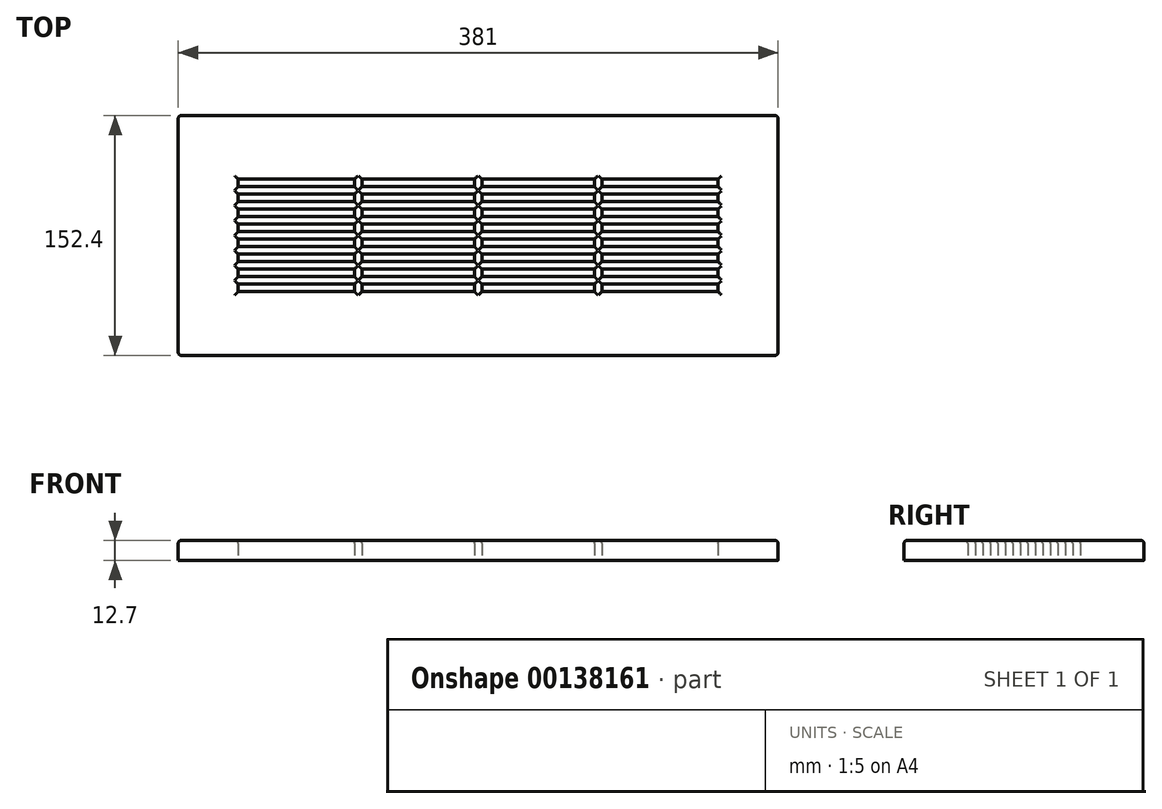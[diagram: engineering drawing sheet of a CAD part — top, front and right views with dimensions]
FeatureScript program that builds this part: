
annotation { "Feature Type Name" : "Feature", "Feature Type Description" : "" }
export const myFeature = defineFeature(function(context is Context, id is Id, definition is map)
    precondition{}
    {
        {
            var Q0;
            Q0=qCreatedBy(makeId("Top.planeOp"),FACE);
            var sketch = newSketch(context, id + "F0", { "sketchPlane" : qUnion([Q0])});
            skLineSegment(sketch, "E0.bottom", {"start": v(-152.4, 38.1) * mm, "end": v(152.4, 38.1) * mm});
            skLineSegment(sketch, "E0.top", {"start": v(-152.4, -38.1) * mm, "end": v(152.4, -38.1) * mm});
            skLineSegment(sketch, "E0.left", {"start": v(-152.4, 38.1) * mm, "end": v(-152.4, -38.1) * mm});
            skLineSegment(sketch, "E0.right", {"start": v(152.4, 38.1) * mm, "end": v(152.4, -38.1) * mm});
            skPoint(sketch, "E0.middle", {"position": v(0, 0) * mm});
            skLineSegment(sketch, "E1.bottom", {"start": v(-190.5, 76.2) * mm, "end": v(190.5, 76.2) * mm});
            skLineSegment(sketch, "E1.top", {"start": v(-190.5, -76.2) * mm, "end": v(190.5, -76.2) * mm});
            skLineSegment(sketch, "E1.left", {"start": v(-190.5, 76.2) * mm, "end": v(-190.5, -76.2) * mm});
            skLineSegment(sketch, "E1.right", {"start": v(190.5, 76.2) * mm, "end": v(190.5, -76.2) * mm});
            skPoint(sketch, "E2", {"position": v(-152.4, 0) * mm});
            skPoint(sketch, "E3", {"position": v(152.4, 0) * mm});
            skPoint(sketch, "E4", {"position": v(-152.4, 19.05) * mm});
            skPoint(sketch, "E5", {"position": v(152.4, 19.05) * mm});
            skPoint(sketch, "E6", {"position": v(-152.4, -19.05) * mm});
            skPoint(sketch, "E7", {"position": v(152.4, -19.05) * mm});
            skLineSegment(sketch, "E8", {"start": v(-152.4, 0) * mm, "end": v(152.4, 0) * mm, "construction": true});
            skLineSegment(sketch, "E9", {"start": v(-152.4, 19.05) * mm, "end": v(152.4, 19.05) * mm, "construction": true});
            skLineSegment(sketch, "E10", {"start": v(-152.4, -19.05) * mm, "end": v(152.4, -19.05) * mm, "construction": true});
            skPoint(sketch, "E11", {"position": v(152.4, 28.58) * mm});
            skPoint(sketch, "E12", {"position": v(-152.4, 28.58) * mm});
            skPoint(sketch, "E13", {"position": v(152.4, 9.53) * mm});
            skPoint(sketch, "E14", {"position": v(-152.4, 9.53) * mm});
            skPoint(sketch, "E15", {"position": v(152.4, -9.53) * mm});
            skPoint(sketch, "E16", {"position": v(-152.4, -9.53) * mm});
            skPoint(sketch, "E17", {"position": v(152.4, -28.58) * mm});
            skPoint(sketch, "E18", {"position": v(-152.4, -28.58) * mm});
            skLineSegment(sketch, "E19", {"start": v(-152.4, 28.58) * mm, "end": v(152.4, 28.58) * mm, "construction": true});
            skLineSegment(sketch, "E20", {"start": v(152.4, 9.53) * mm, "end": v(-152.4, 9.53) * mm, "construction": true});
            skLineSegment(sketch, "E21", {"start": v(-152.4, -9.53) * mm, "end": v(152.4, -9.53) * mm, "construction": true});
            skLineSegment(sketch, "E22", {"start": v(152.4, -28.58) * mm, "end": v(-152.4, -28.58) * mm, "construction": true});
            skPoint(sketch, "E23", {"position": v(-152.4, 30.96) * mm});
            skPoint(sketch, "E24", {"position": v(152.4, 30.96) * mm});
            skPoint(sketch, "E25", {"position": v(152.4, 26.2) * mm});
            skPoint(sketch, "E26", {"position": v(-152.4, 26.2) * mm});
            skLineSegment(sketch, "E27", {"start": v(-152.4, 30.96) * mm, "end": v(152.4, 30.96) * mm});
            skLineSegment(sketch, "E28", {"start": v(-152.4, 26.2) * mm, "end": v(152.4, 26.2) * mm});
            skPoint(sketch, "E29", {"position": v(152.4, 21.43) * mm});
            skPoint(sketch, "E30", {"position": v(-152.4, 21.43) * mm});
            skPoint(sketch, "E31", {"position": v(152.4, 16.67) * mm});
            skPoint(sketch, "E32", {"position": v(-152.4, 16.67) * mm});
            skLineSegment(sketch, "E33", {"start": v(-152.4, 21.43) * mm, "end": v(152.4, 21.43) * mm});
            skLineSegment(sketch, "E34", {"start": v(152.4, 16.67) * mm, "end": v(-152.4, 16.67) * mm});
            skPoint(sketch, "E35", {"position": v(152.4, 11.9) * mm});
            skPoint(sketch, "E36", {"position": v(-152.4, 11.9) * mm});
            skPoint(sketch, "E37", {"position": v(-152.4, 7.14) * mm});
            skPoint(sketch, "E38", {"position": v(152.4, 7.14) * mm});
            skPoint(sketch, "E39", {"position": v(152.4, -2.38) * mm});
            skPoint(sketch, "E40", {"position": v(-152.4, -2.38) * mm});
            skPoint(sketch, "E41", {"position": v(-152.4, -11.9) * mm});
            skPoint(sketch, "E42", {"position": v(152.4, -11.9) * mm});
            skPoint(sketch, "E43", {"position": v(152.4, -21.43) * mm});
            skPoint(sketch, "E44", {"position": v(-152.4, -21.43) * mm});
            skPoint(sketch, "E45", {"position": v(-152.4, -30.96) * mm});
            skPoint(sketch, "E46", {"position": v(152.4, -30.96) * mm});
            skPoint(sketch, "E47", {"position": v(152.4, 2.38) * mm});
            skPoint(sketch, "E48", {"position": v(-152.4, 2.38) * mm});
            skPoint(sketch, "E49", {"position": v(-152.4, -7.14) * mm});
            skPoint(sketch, "E50", {"position": v(152.4, -7.14) * mm});
            skPoint(sketch, "E51", {"position": v(152.4, -16.67) * mm});
            skPoint(sketch, "E52", {"position": v(-152.4, -16.67) * mm});
            skPoint(sketch, "E53", {"position": v(-152.4, -26.2) * mm});
            skPoint(sketch, "E54", {"position": v(152.4, -26.2) * mm});
            skLineSegment(sketch, "E55", {"start": v(152.4, 11.9) * mm, "end": v(-152.4, 11.9) * mm});
            skLineSegment(sketch, "E56", {"start": v(-152.4, 7.14) * mm, "end": v(152.4, 7.14) * mm});
            skLineSegment(sketch, "E57", {"start": v(152.4, 2.38) * mm, "end": v(-152.4, 2.38) * mm});
            skLineSegment(sketch, "E58", {"start": v(-152.4, -2.38) * mm, "end": v(152.4, -2.38) * mm});
            skLineSegment(sketch, "E59", {"start": v(152.4, -7.14) * mm, "end": v(-152.4, -7.14) * mm});
            skLineSegment(sketch, "E60", {"start": v(-152.4, -11.9) * mm, "end": v(152.4, -11.9) * mm});
            skLineSegment(sketch, "E61", {"start": v(152.4, -16.67) * mm, "end": v(-152.4, -16.67) * mm});
            skLineSegment(sketch, "E62", {"start": v(-152.4, -21.43) * mm, "end": v(152.4, -21.43) * mm});
            skLineSegment(sketch, "E63", {"start": v(152.4, -26.2) * mm, "end": v(-152.4, -26.2) * mm});
            skLineSegment(sketch, "E64", {"start": v(-152.4, -30.96) * mm, "end": v(152.4, -30.96) * mm});
            skPoint(sketch, "E65", {"position": v(-152.4, 35.72) * mm});
            skPoint(sketch, "E66", {"position": v(152.4, 35.72) * mm});
            skPoint(sketch, "E67", {"position": v(152.4, -35.72) * mm});
            skPoint(sketch, "E68", {"position": v(-152.4, -35.72) * mm});
            skLineSegment(sketch, "E69", {"start": v(152.4, 35.72) * mm, "end": v(-152.4, 35.72) * mm});
            skLineSegment(sketch, "E70", {"start": v(-152.4, -35.72) * mm, "end": v(152.4, -35.72) * mm});
            skPoint(sketch, "E71", {"position": v(0, 38.1) * mm});
            skPoint(sketch, "E72", {"position": v(0, -38.1) * mm});
            skLineSegment(sketch, "E73", {"start": v(0, 38.1) * mm, "end": v(0, -38.1) * mm, "construction": true});
            skPoint(sketch, "E74", {"position": v(2.38, 38.1) * mm});
            skPoint(sketch, "E75", {"position": v(2.38, -38.1) * mm});
            skPoint(sketch, "E76", {"position": v(-2.38, -38.1) * mm});
            skPoint(sketch, "E77", {"position": v(-2.38, 38.1) * mm});
            skLineSegment(sketch, "E78", {"start": v(-2.38, 38.1) * mm, "end": v(-2.38, -38.1) * mm});
            skLineSegment(sketch, "E79", {"start": v(2.38, 38.1) * mm, "end": v(2.38, -38.1) * mm});
            skPoint(sketch, "E80", {"position": v(76.2, 38.1) * mm});
            skPoint(sketch, "E81", {"position": v(76.2, -38.1) * mm});
            skPoint(sketch, "E82", {"position": v(-76.2, -38.1) * mm});
            skPoint(sketch, "E83", {"position": v(-76.2, 38.1) * mm});
            skPoint(sketch, "E84", {"position": v(-78.58, 38.1) * mm});
            skPoint(sketch, "E85", {"position": v(-78.58, -38.1) * mm});
            skPoint(sketch, "E86", {"position": v(-73.82, 38.1) * mm});
            skPoint(sketch, "E87", {"position": v(-73.82, -38.1) * mm});
            skPoint(sketch, "E88", {"position": v(73.82, 38.1) * mm});
            skPoint(sketch, "E89", {"position": v(73.82, -38.1) * mm});
            skPoint(sketch, "E90", {"position": v(78.58, 38.1) * mm});
            skPoint(sketch, "E91", {"position": v(78.58, -38.1) * mm});
            skLineSegment(sketch, "E92", {"start": v(-78.58, 38.1) * mm, "end": v(-78.58, -38.1) * mm});
            skLineSegment(sketch, "E93", {"start": v(-73.82, 38.1) * mm, "end": v(-73.82, -38.1) * mm});
            skLineSegment(sketch, "E94", {"start": v(73.82, 38.1) * mm, "end": v(73.82, -38.1) * mm});
            skLineSegment(sketch, "E95", {"start": v(78.58, 38.1) * mm, "end": v(78.58, -38.1) * mm});
            skSolve(sketch);
        }
        {
            var Q0;
            {var subQ7=sQuery(id+"F0.wireOp",EDGE,"E0.bottom");Q0=makeQuery(id+"F0.imprint","IMPRINT",FACE,{"disambiguationData":[TD([[makeQuery(id+"F0.imprint","IMPRINT",EDGE,{"derivedFrom":subQ7}),1.0]])]});}
            var Q1;
            {var subQ0=sQuery(id+"F0.wireOp",EDGE,"E0.bottom");Q1=makeQuery(id+"F0.imprint","IMPRINT",FACE,{"disambiguationData":[TD([[makeQuery(id+"F0.imprint","IMPRINT",EDGE,{"derivedFrom":subQ0}),-1.0]])]});}
            var Q2;
            {var subQ0=sQuery(id+"F0.wireOp",EDGE,"E0.top");Q2=makeQuery(id+"F0.imprint","IMPRINT",FACE,{"disambiguationData":[TD([[makeQuery(id+"F0.imprint","IMPRINT",EDGE,{"derivedFrom":subQ0}),1.0]])]});}
            var Q3;
            {var subQ0=sQuery(id+"F0.wireOp",EDGE,"E63");Q3=makeQuery(id+"F0.imprint","IMPRINT",FACE,{"disambiguationData":[TD([[makeQuery(id+"F0.imprint","IMPRINT",EDGE,{"derivedFrom":subQ0}),1.0]])]});}
            var Q4;
            {var subQ0=sQuery(id+"F0.wireOp",EDGE,"E61");Q4=makeQuery(id+"F0.imprint","IMPRINT",FACE,{"disambiguationData":[TD([[makeQuery(id+"F0.imprint","IMPRINT",EDGE,{"derivedFrom":subQ0}),1.0]])]});}
            var Q5;
            {var subQ0=sQuery(id+"F0.wireOp",EDGE,"E59");Q5=makeQuery(id+"F0.imprint","IMPRINT",FACE,{"disambiguationData":[TD([[makeQuery(id+"F0.imprint","IMPRINT",EDGE,{"derivedFrom":subQ0}),1.0]])]});}
            var Q6;
            {var subQ0=sQuery(id+"F0.wireOp",EDGE,"E57");Q6=makeQuery(id+"F0.imprint","IMPRINT",FACE,{"disambiguationData":[TD([[makeQuery(id+"F0.imprint","IMPRINT",EDGE,{"derivedFrom":subQ0}),1.0]])]});}
            var Q7;
            {var subQ0=sQuery(id+"F0.wireOp",EDGE,"E55");Q7=makeQuery(id+"F0.imprint","IMPRINT",FACE,{"disambiguationData":[TD([[makeQuery(id+"F0.imprint","IMPRINT",EDGE,{"derivedFrom":subQ0}),1.0]])]});}
            var Q8;
            {var subQ0=sQuery(id+"F0.wireOp",EDGE,"E33");Q8=makeQuery(id+"F0.imprint","IMPRINT",FACE,{"disambiguationData":[TD([[makeQuery(id+"F0.imprint","IMPRINT",EDGE,{"derivedFrom":subQ0}),-1.0]])]});}
            var Q9;
            {var subQ0=sQuery(id+"F0.wireOp",EDGE,"E27");Q9=makeQuery(id+"F0.imprint","IMPRINT",FACE,{"disambiguationData":[TD([[makeQuery(id+"F0.imprint","IMPRINT",EDGE,{"derivedFrom":subQ0}),-1.0]])]});}
            var Q10;
            {var subQ0=sQuery(id+"F0.wireOp",EDGE,"E92");var subQ1=sQuery(id+"F0.wireOp",EDGE,"E27");var subQ2=makeQuery(id+"F0.imprint","INTERSECT",VERTEX,{"derivedFrom":[subQ1,subQ0]});Q10=makeQuery(id+"F0.imprint","IMPRINT",FACE,{"disambiguationData":[TD([[makeQuery(id+"F0.imprint","IMPRINT",EDGE,{"disambiguationData":[TD([[subQ2,-1.0]])],"derivedFrom":subQ1}),1.0]])]});}
            var Q11;
            {var subQ0=sQuery(id+"F0.wireOp",EDGE,"E92");var subQ1=sQuery(id+"F0.wireOp",EDGE,"E28");var subQ2=makeQuery(id+"F0.imprint","INTERSECT",VERTEX,{"derivedFrom":[subQ1,subQ0]});Q11=makeQuery(id+"F0.imprint","IMPRINT",FACE,{"disambiguationData":[TD([[makeQuery(id+"F0.imprint","IMPRINT",EDGE,{"disambiguationData":[TD([[subQ2,-1.0]])],"derivedFrom":subQ1}),-1.0]])]});}
            var Q12;
            {var subQ0=sQuery(id+"F0.wireOp",EDGE,"E93");var subQ1=sQuery(id+"F0.wireOp",EDGE,"E34");var subQ2=makeQuery(id+"F0.imprint","INTERSECT",VERTEX,{"derivedFrom":[subQ1,subQ0]});Q12=makeQuery(id+"F0.imprint","IMPRINT",FACE,{"disambiguationData":[TD([[makeQuery(id+"F0.imprint","IMPRINT",EDGE,{"disambiguationData":[TD([[subQ2,-1.0]])],"derivedFrom":subQ1}),1.0]])]});}
            var Q13;
            {var subQ0=sQuery(id+"F0.wireOp",EDGE,"E92");var subQ1=sQuery(id+"F0.wireOp",EDGE,"E56");var subQ2=makeQuery(id+"F0.imprint","INTERSECT",VERTEX,{"derivedFrom":[subQ1,subQ0]});Q13=makeQuery(id+"F0.imprint","IMPRINT",FACE,{"disambiguationData":[TD([[makeQuery(id+"F0.imprint","IMPRINT",EDGE,{"disambiguationData":[TD([[subQ2,-1.0]])],"derivedFrom":subQ1}),-1.0]])]});}
            var Q14;
            {var subQ0=sQuery(id+"F0.wireOp",EDGE,"E92");var subQ1=sQuery(id+"F0.wireOp",EDGE,"E58");var subQ2=makeQuery(id+"F0.imprint","INTERSECT",VERTEX,{"derivedFrom":[subQ1,subQ0]});Q14=makeQuery(id+"F0.imprint","IMPRINT",FACE,{"disambiguationData":[TD([[makeQuery(id+"F0.imprint","IMPRINT",EDGE,{"disambiguationData":[TD([[subQ2,-1.0]])],"derivedFrom":subQ1}),-1.0]])]});}
            var Q15;
            {var subQ0=sQuery(id+"F0.wireOp",EDGE,"E92");var subQ1=sQuery(id+"F0.wireOp",EDGE,"E60");var subQ2=makeQuery(id+"F0.imprint","INTERSECT",VERTEX,{"derivedFrom":[subQ1,subQ0]});Q15=makeQuery(id+"F0.imprint","IMPRINT",FACE,{"disambiguationData":[TD([[makeQuery(id+"F0.imprint","IMPRINT",EDGE,{"disambiguationData":[TD([[subQ2,-1.0]])],"derivedFrom":subQ1}),-1.0]])]});}
            var Q16;
            {var subQ0=sQuery(id+"F0.wireOp",EDGE,"E92");var subQ1=sQuery(id+"F0.wireOp",EDGE,"E62");var subQ2=makeQuery(id+"F0.imprint","INTERSECT",VERTEX,{"derivedFrom":[subQ1,subQ0]});Q16=makeQuery(id+"F0.imprint","IMPRINT",FACE,{"disambiguationData":[TD([[makeQuery(id+"F0.imprint","IMPRINT",EDGE,{"disambiguationData":[TD([[subQ2,-1.0]])],"derivedFrom":subQ1}),-1.0]])]});}
            var Q17;
            {var subQ0=sQuery(id+"F0.wireOp",EDGE,"E92");var subQ1=sQuery(id+"F0.wireOp",EDGE,"E64");var subQ2=makeQuery(id+"F0.imprint","INTERSECT",VERTEX,{"derivedFrom":[subQ1,subQ0]});Q17=makeQuery(id+"F0.imprint","IMPRINT",FACE,{"disambiguationData":[TD([[makeQuery(id+"F0.imprint","IMPRINT",EDGE,{"disambiguationData":[TD([[subQ2,-1.0]])],"derivedFrom":subQ1}),-1.0]])]});}
            var Q18;
            {var subQ0=sQuery(id+"F0.wireOp",EDGE,"E78");var subQ1=sQuery(id+"F0.wireOp",EDGE,"E64");var subQ2=makeQuery(id+"F0.imprint","INTERSECT",VERTEX,{"derivedFrom":[subQ1,subQ0]});Q18=makeQuery(id+"F0.imprint","IMPRINT",FACE,{"disambiguationData":[TD([[makeQuery(id+"F0.imprint","IMPRINT",EDGE,{"disambiguationData":[TD([[subQ2,-1.0]])],"derivedFrom":subQ1}),-1.0]])]});}
            var Q19;
            {var subQ0=sQuery(id+"F0.wireOp",EDGE,"E78");var subQ1=sQuery(id+"F0.wireOp",EDGE,"E62");var subQ2=makeQuery(id+"F0.imprint","INTERSECT",VERTEX,{"derivedFrom":[subQ1,subQ0]});Q19=makeQuery(id+"F0.imprint","IMPRINT",FACE,{"disambiguationData":[TD([[makeQuery(id+"F0.imprint","IMPRINT",EDGE,{"disambiguationData":[TD([[subQ2,-1.0]])],"derivedFrom":subQ1}),-1.0]])]});}
            var Q20;
            {var subQ0=sQuery(id+"F0.wireOp",EDGE,"E79");var subQ1=sQuery(id+"F0.wireOp",EDGE,"E34");var subQ2=makeQuery(id+"F0.imprint","INTERSECT",VERTEX,{"derivedFrom":[subQ1,subQ0]});Q20=makeQuery(id+"F0.imprint","IMPRINT",FACE,{"disambiguationData":[TD([[makeQuery(id+"F0.imprint","IMPRINT",EDGE,{"disambiguationData":[TD([[subQ2,-1.0]])],"derivedFrom":subQ1}),1.0]])]});}
            var Q21;
            {var subQ0=sQuery(id+"F0.wireOp",EDGE,"E78");var subQ1=sQuery(id+"F0.wireOp",EDGE,"E28");var subQ2=makeQuery(id+"F0.imprint","INTERSECT",VERTEX,{"derivedFrom":[subQ1,subQ0]});Q21=makeQuery(id+"F0.imprint","IMPRINT",FACE,{"disambiguationData":[TD([[makeQuery(id+"F0.imprint","IMPRINT",EDGE,{"disambiguationData":[TD([[subQ2,-1.0]])],"derivedFrom":subQ1}),-1.0]])]});}
            var Q22;
            {var subQ0=sQuery(id+"F0.wireOp",EDGE,"E78");var subQ1=sQuery(id+"F0.wireOp",EDGE,"E27");var subQ2=makeQuery(id+"F0.imprint","INTERSECT",VERTEX,{"derivedFrom":[subQ1,subQ0]});Q22=makeQuery(id+"F0.imprint","IMPRINT",FACE,{"disambiguationData":[TD([[makeQuery(id+"F0.imprint","IMPRINT",EDGE,{"disambiguationData":[TD([[subQ2,-1.0]])],"derivedFrom":subQ1}),1.0]])]});}
            var Q23;
            {var subQ0=sQuery(id+"F0.wireOp",EDGE,"E94");var subQ1=sQuery(id+"F0.wireOp",EDGE,"E27");var subQ2=makeQuery(id+"F0.imprint","INTERSECT",VERTEX,{"derivedFrom":[subQ1,subQ0]});Q23=makeQuery(id+"F0.imprint","IMPRINT",FACE,{"disambiguationData":[TD([[makeQuery(id+"F0.imprint","IMPRINT",EDGE,{"disambiguationData":[TD([[subQ2,-1.0]])],"derivedFrom":subQ1}),1.0]])]});}
            var Q24;
            {var subQ0=sQuery(id+"F0.wireOp",EDGE,"E94");var subQ1=sQuery(id+"F0.wireOp",EDGE,"E28");var subQ2=makeQuery(id+"F0.imprint","INTERSECT",VERTEX,{"derivedFrom":[subQ1,subQ0]});Q24=makeQuery(id+"F0.imprint","IMPRINT",FACE,{"disambiguationData":[TD([[makeQuery(id+"F0.imprint","IMPRINT",EDGE,{"disambiguationData":[TD([[subQ2,-1.0]])],"derivedFrom":subQ1}),-1.0]])]});}
            var Q25;
            {var subQ0=sQuery(id+"F0.wireOp",EDGE,"E95");var subQ1=sQuery(id+"F0.wireOp",EDGE,"E34");var subQ2=makeQuery(id+"F0.imprint","INTERSECT",VERTEX,{"derivedFrom":[subQ1,subQ0]});Q25=makeQuery(id+"F0.imprint","IMPRINT",FACE,{"disambiguationData":[TD([[makeQuery(id+"F0.imprint","IMPRINT",EDGE,{"disambiguationData":[TD([[subQ2,-1.0]])],"derivedFrom":subQ1}),1.0]])]});}
            var Q26;
            {var subQ0=sQuery(id+"F0.wireOp",EDGE,"E94");var subQ1=sQuery(id+"F0.wireOp",EDGE,"E56");var subQ2=makeQuery(id+"F0.imprint","INTERSECT",VERTEX,{"derivedFrom":[subQ1,subQ0]});Q26=makeQuery(id+"F0.imprint","IMPRINT",FACE,{"disambiguationData":[TD([[makeQuery(id+"F0.imprint","IMPRINT",EDGE,{"disambiguationData":[TD([[subQ2,-1.0]])],"derivedFrom":subQ1}),-1.0]])]});}
            var Q27;
            {var subQ0=sQuery(id+"F0.wireOp",EDGE,"E94");var subQ1=sQuery(id+"F0.wireOp",EDGE,"E58");var subQ2=makeQuery(id+"F0.imprint","INTERSECT",VERTEX,{"derivedFrom":[subQ1,subQ0]});Q27=makeQuery(id+"F0.imprint","IMPRINT",FACE,{"disambiguationData":[TD([[makeQuery(id+"F0.imprint","IMPRINT",EDGE,{"disambiguationData":[TD([[subQ2,-1.0]])],"derivedFrom":subQ1}),-1.0]])]});}
            var Q28;
            {var subQ0=sQuery(id+"F0.wireOp",EDGE,"E94");var subQ1=sQuery(id+"F0.wireOp",EDGE,"E60");var subQ2=makeQuery(id+"F0.imprint","INTERSECT",VERTEX,{"derivedFrom":[subQ1,subQ0]});Q28=makeQuery(id+"F0.imprint","IMPRINT",FACE,{"disambiguationData":[TD([[makeQuery(id+"F0.imprint","IMPRINT",EDGE,{"disambiguationData":[TD([[subQ2,-1.0]])],"derivedFrom":subQ1}),-1.0]])]});}
            var Q29;
            {var subQ0=sQuery(id+"F0.wireOp",EDGE,"E94");var subQ1=sQuery(id+"F0.wireOp",EDGE,"E62");var subQ2=makeQuery(id+"F0.imprint","INTERSECT",VERTEX,{"derivedFrom":[subQ1,subQ0]});Q29=makeQuery(id+"F0.imprint","IMPRINT",FACE,{"disambiguationData":[TD([[makeQuery(id+"F0.imprint","IMPRINT",EDGE,{"disambiguationData":[TD([[subQ2,-1.0]])],"derivedFrom":subQ1}),-1.0]])]});}
            var Q30;
            {var subQ0=sQuery(id+"F0.wireOp",EDGE,"E94");var subQ1=sQuery(id+"F0.wireOp",EDGE,"E64");var subQ2=makeQuery(id+"F0.imprint","INTERSECT",VERTEX,{"derivedFrom":[subQ1,subQ0]});Q30=makeQuery(id+"F0.imprint","IMPRINT",FACE,{"disambiguationData":[TD([[makeQuery(id+"F0.imprint","IMPRINT",EDGE,{"disambiguationData":[TD([[subQ2,-1.0]])],"derivedFrom":subQ1}),-1.0]])]});}
            var Q31;
            {var subQ0=sQuery(id+"F0.wireOp",EDGE,"E78");var subQ1=sQuery(id+"F0.wireOp",EDGE,"E56");var subQ2=makeQuery(id+"F0.imprint","INTERSECT",VERTEX,{"derivedFrom":[subQ1,subQ0]});Q31=makeQuery(id+"F0.imprint","IMPRINT",FACE,{"disambiguationData":[TD([[makeQuery(id+"F0.imprint","IMPRINT",EDGE,{"disambiguationData":[TD([[subQ2,-1.0]])],"derivedFrom":subQ1}),-1.0]])]});}
            var Q32;
            {var subQ0=sQuery(id+"F0.wireOp",EDGE,"E78");var subQ1=sQuery(id+"F0.wireOp",EDGE,"E58");var subQ2=makeQuery(id+"F0.imprint","INTERSECT",VERTEX,{"derivedFrom":[subQ1,subQ0]});Q32=makeQuery(id+"F0.imprint","IMPRINT",FACE,{"disambiguationData":[TD([[makeQuery(id+"F0.imprint","IMPRINT",EDGE,{"disambiguationData":[TD([[subQ2,-1.0]])],"derivedFrom":subQ1}),-1.0]])]});}
            var Q33;
            {var subQ0=sQuery(id+"F0.wireOp",EDGE,"E78");var subQ1=sQuery(id+"F0.wireOp",EDGE,"E60");var subQ2=makeQuery(id+"F0.imprint","INTERSECT",VERTEX,{"derivedFrom":[subQ1,subQ0]});Q33=makeQuery(id+"F0.imprint","IMPRINT",FACE,{"disambiguationData":[TD([[makeQuery(id+"F0.imprint","IMPRINT",EDGE,{"disambiguationData":[TD([[subQ2,-1.0]])],"derivedFrom":subQ1}),-1.0]])]});}
            extrude(context, id + "F1", {"entities" : qUnion([Q0, Q1, Q2, Q3, Q4, Q5, Q6, Q7, Q8, Q9, Q10, Q11, Q12, Q13, Q14, Q15, Q16, Q17, Q18, Q19, Q20, Q21, Q22, Q23, Q24, Q25, Q26, Q27, Q28, Q29, Q30, Q31, Q32, Q33]), "depth" : 12.7 * mm, "offsetDistance" : 25 * mm});
        }
        {
            var Q0;
            Q0=makeQuery(id+"F1.opExtrude","CAP_FACE",FACE,{"disambiguationData":[OSD([sQuery(id+"F0.wireOp",EDGE,"E0.left"),sQuery(id+"F0.wireOp",EDGE,"E0.right"),sQuery(id+"F0.wireOp",EDGE,"E1.bottom"),sQuery(id+"F0.wireOp",EDGE,"E1.top"),sQuery(id+"F0.wireOp",EDGE,"E1.left"),sQuery(id+"F0.wireOp",EDGE,"E1.right"),sQuery(id+"F0.wireOp",EDGE,"E27"),sQuery(id+"F0.wireOp",EDGE,"E28"),sQuery(id+"F0.wireOp",EDGE,"E33"),sQuery(id+"F0.wireOp",EDGE,"E34"),sQuery(id+"F0.wireOp",EDGE,"E55"),sQuery(id+"F0.wireOp",EDGE,"E56"),sQuery(id+"F0.wireOp",EDGE,"E57"),sQuery(id+"F0.wireOp",EDGE,"E58"),sQuery(id+"F0.wireOp",EDGE,"E59"),sQuery(id+"F0.wireOp",EDGE,"E60"),sQuery(id+"F0.wireOp",EDGE,"E61"),sQuery(id+"F0.wireOp",EDGE,"E62"),sQuery(id+"F0.wireOp",EDGE,"E63"),sQuery(id+"F0.wireOp",EDGE,"E64"),sQuery(id+"F0.wireOp",EDGE,"E69"),sQuery(id+"F0.wireOp",EDGE,"E70"),sQuery(id+"F0.wireOp",EDGE,"E78"),sQuery(id+"F0.wireOp",EDGE,"E79"),sQuery(id+"F0.wireOp",EDGE,"E92"),sQuery(id+"F0.wireOp",EDGE,"E93"),sQuery(id+"F0.wireOp",EDGE,"E94"),sQuery(id+"F0.wireOp",EDGE,"E95")])],"isStart":false});
            var Q1;
            Q1=makeQuery(id+"F1.opExtrude","SWEPT_EDGE",EDGE,{"disambiguationData":[OSD([sQuery(id+"F0.wireOp",EDGE,"E1.bottom"),sQuery(id+"F0.wireOp",EDGE,"E1.left")])]});
            var Q2;
            Q2=makeQuery(id+"F1.opExtrude","SWEPT_EDGE",EDGE,{"disambiguationData":[OSD([sQuery(id+"F0.wireOp",EDGE,"E1.bottom"),sQuery(id+"F0.wireOp",EDGE,"E1.right")])]});
            var Q3;
            Q3=makeQuery(id+"F1.opExtrude","SWEPT_EDGE",EDGE,{"disambiguationData":[OSD([sQuery(id+"F0.wireOp",EDGE,"E1.top"),sQuery(id+"F0.wireOp",EDGE,"E1.right")])]});
            var Q4;
            Q4=makeQuery(id+"F1.opExtrude","SWEPT_EDGE",EDGE,{"disambiguationData":[OSD([sQuery(id+"F0.wireOp",EDGE,"E1.top"),sQuery(id+"F0.wireOp",EDGE,"E1.left")])]});
            fillet(context, id + "F2", {"entities" : qUnion([Q0, Q1, Q2, Q3, Q4]), "tangentPropagation" : true, "radius" : 2 * mm, "defaultsChanged" : false, "vertexSettings" : [], "allowEdgeOverflow" : false});
        }
    });
